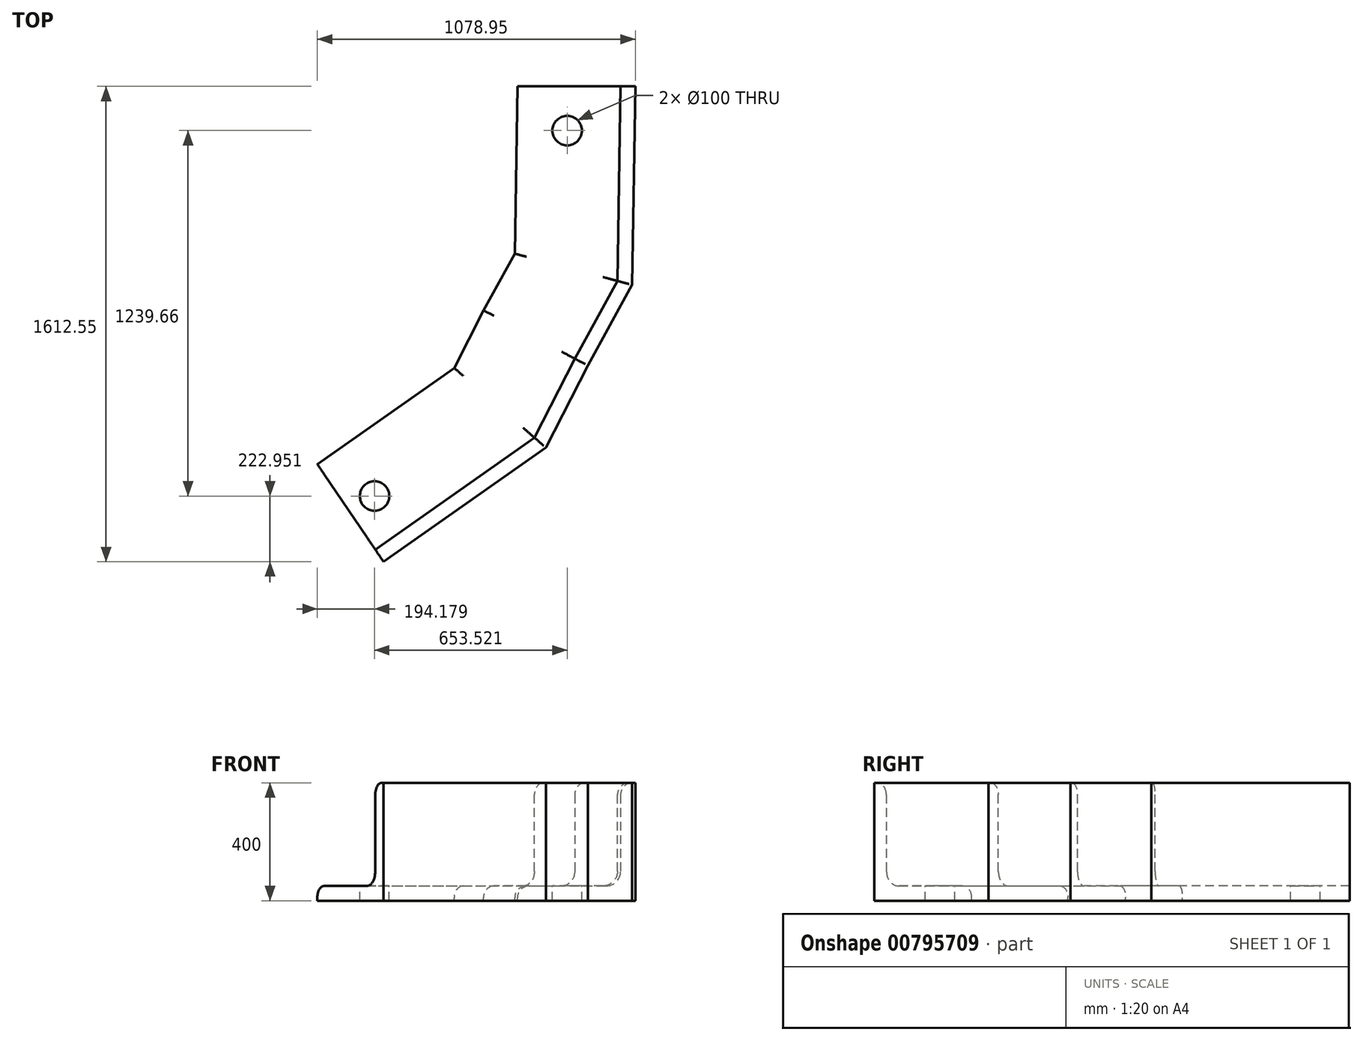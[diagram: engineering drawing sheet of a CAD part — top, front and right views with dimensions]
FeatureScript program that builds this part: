
annotation { "Feature Type Name" : "Feature", "Feature Type Description" : "" }
export const myFeature = defineFeature(function(context is Context, id is Id, definition is map)
    precondition{}
    {
        {
            var Q0;
            Q0=qCreatedBy(makeId("Front.planeOp"),FACE);
            var sketch = newSketch(context, id + "F0", { "sketchPlane" : qUnion([Q0])});
            skLineSegment(sketch, "E0", {"start": v(-836.52, 148.24) * mm, "end": v(-436.52, 148.24) * mm});
            skLineSegment(sketch, "E1", {"start": v(-436.52, 548.24) * mm, "end": v(-436.52, 148.24) * mm});
            skLineSegment(sketch, "E2.0", {"start": v(-796.52, 198.24) * mm, "end": v(-536.52, 198.24) * mm});
            skLineSegment(sketch, "E2.1", {"start": v(-486.52, 508.24) * mm, "end": v(-486.52, 248.24) * mm});
            skLineSegment(sketch, "E3", {"start": v(-436.52, 548.24) * mm, "end": v(-446.52, 548.24) * mm});
            skPoint(sketch, "E4.visualSharp", {"position": v(-486.52, 548.24) * mm});
            skArc(sketch, "E4.filletArc", {"start": v(-446.52, 548.24) * mm, "mid": v(-474.8, 536.53) * mm, "end": v(-486.52, 508.24) * mm});
            skLineSegment(sketch, "E5", {"start": v(-836.52, 148.24) * mm, "end": v(-836.52, 158.24) * mm});
            skPoint(sketch, "E6.visualSharp", {"position": v(-836.52, 198.24) * mm});
            skArc(sketch, "E6.filletArc", {"start": v(-796.52, 198.24) * mm, "mid": v(-824.8, 186.53) * mm, "end": v(-836.52, 158.24) * mm});
            skPoint(sketch, "E7.visualSharp", {"position": v(-486.52, 198.24) * mm});
            skArc(sketch, "E7.filletArc", {"start": v(-536.52, 198.24) * mm, "mid": v(-501.16, 212.89) * mm, "end": v(-486.52, 248.24) * mm});
            skSolve(sketch);
        }
        {
            var Q0;
            Q0=qCreatedBy(makeId("Top.planeOp"),FACE);
            var sketch = newSketch(context, id + "F1", { "sketchPlane" : qUnion([Q0])});
            skLineSegment(sketch, "E8", {"start": v(-107.32, -226.62) * mm, "end": v(-115.97, -761.25) * mm});
            skLineSegment(sketch, "E9", {"start": v(-115.97, -761.25) * mm, "end": v(-413.35, -1301.29) * mm});
            skSolve(sketch);
        }
        {
            var Q0;
            Q0 = qSketchRegion(id + "F0", true);
            var Q1;
            Q1 = qConstructionFilter(qBodyType(qCreatedBy(id + "F1" ,EDGE), BodyType.WIRE), ConstructionObject.NO);
            sweep(context, id + "F2", {"profiles" : qUnion([Q0]), "path" : qUnion([Q1])});
        }
        {
            var Q0;
            Q0=makeQuery(id+"F2.opSweep","SWEPT_BODY",BODY,{"disambiguationData":[OSD([sQuery(id+"F0.wireOp",EDGE,"E0"),sQuery(id+"F0.wireOp",EDGE,"E1"),sQuery(id+"F0.wireOp",EDGE,"E2.0"),sQuery(id+"F0.wireOp",EDGE,"E2.1"),sQuery(id+"F0.wireOp",EDGE,"E3"),sQuery(id+"F0.wireOp",EDGE,"E4.filletArc"),sQuery(id+"F0.wireOp",EDGE,"E5"),sQuery(id+"F0.wireOp",EDGE,"E6.filletArc"),sQuery(id+"F0.wireOp",EDGE,"E7.filletArc"),sQuery(id+"F1.wireOp",EDGE,"E9")])]});
            var Q1;
            Q1=makeQuery(id+"F2.opSweep","CAP_FACE",FACE,{"disambiguationData":[OSD([sQuery(id+"F0.wireOp",EDGE,"E0"),sQuery(id+"F0.wireOp",EDGE,"E1"),sQuery(id+"F0.wireOp",EDGE,"E2.0"),sQuery(id+"F0.wireOp",EDGE,"E2.1"),sQuery(id+"F0.wireOp",EDGE,"E3"),sQuery(id+"F0.wireOp",EDGE,"E4.filletArc"),sQuery(id+"F0.wireOp",EDGE,"E5"),sQuery(id+"F0.wireOp",EDGE,"E6.filletArc"),sQuery(id+"F0.wireOp",EDGE,"E7.filletArc"),sQuery(id+"F1.wireOp",VERTEX,"E9.end")])],"isStart":false});
            mirror(context, id + "F3", {"operationType" : NewBodyOperationType.ADD, "entities" : qUnion([Q0]), "mirrorPlane" : qUnion([Q1])});
        }
        {
            var Q0;
            {var subQ0=makeQuery(id+"F2.opSweep","SWEPT_FACE",FACE,{"disambiguationData":[OSD([sQuery(id+"F0.wireOp",EDGE,"E2.0"),sQuery(id+"F1.wireOp",EDGE,"E8")])]});Q0=makeQuery(id+"F3.boolean.opBoolean","MERGE",FACE,{"derivedFrom":[subQ0,makeQuery(id+"F3.opPattern","COPY",FACE,{"derivedFrom":subQ0,"instanceName":"1"})]});}
            var sketch = newSketch(context, id + "F4", { "sketchPlane" : qUnion([Q0])});
            skCircle(sketch, "E10", {"center": v(-667.77, -149.94) * mm, "radius": 50 * mm});
            skSolve(sketch);
        }
        {
            var Q0;
            Q0=sQuery(id+"F4.wireOp",VERTEX,"E10.center");
            var Q1;
            Q1=makeQuery(id+"F2.opSweep","SWEPT_BODY",BODY,{"disambiguationData":[OSD([sQuery(id+"F0.wireOp",EDGE,"E0"),sQuery(id+"F0.wireOp",EDGE,"E1"),sQuery(id+"F0.wireOp",EDGE,"E2.0"),sQuery(id+"F0.wireOp",EDGE,"E2.1"),sQuery(id+"F0.wireOp",EDGE,"E3"),sQuery(id+"F0.wireOp",EDGE,"E4.filletArc"),sQuery(id+"F0.wireOp",EDGE,"E5"),sQuery(id+"F0.wireOp",EDGE,"E6.filletArc"),sQuery(id+"F0.wireOp",EDGE,"E7.filletArc"),sQuery(id+"F1.wireOp",EDGE,"E9")])]});
            hole(context, id + "F5", {"style" : HoleStyle.SIMPLE, "endStyle" : HoleEndStyle.THROUGH, "holeDiameter" : 100 * mm, "majorDiameter" : 5 * mm, "isTappedThrough" : true, "tappedDepth" : 12 * mm, "tapClearance" : 3, "locations" : qUnion([Q0]), "scope" : qUnion([Q1])});
        }
        {
            var Q0;
            {var subQ0=makeQuery(id+"F2.opSweep","SWEPT_FACE",FACE,{"disambiguationData":[OSD([sQuery(id+"F0.wireOp",EDGE,"E2.0"),sQuery(id+"F1.wireOp",EDGE,"E8")])]});Q0=makeQuery(id+"F3.boolean.opBoolean","MERGE",FACE,{"derivedFrom":[subQ0,makeQuery(id+"F3.opPattern","COPY",FACE,{"derivedFrom":subQ0,"instanceName":"1"})]});}
            var sketch = newSketch(context, id + "F6", { "sketchPlane" : qUnion([Q0])});
            skLineSegment(sketch, "E11.0", {"start": v(-1321.3, -1389.6) * mm, "end": v(-936.27, -1118.99) * mm});
            skSolve(sketch);
        }
        {
            var Q0;
            Q0=sQuery(id+"F6.wireOp",VERTEX,"3796be69-d90f-4293-91cc-07bbf22c86ba.0.start");
            var Q1;
            Q1=sQuery(id+"F6.wireOp",VERTEX,"E11.0.start");
            var Q2;
            Q2=makeQuery(id+"F2.opSweep","SWEPT_BODY",BODY,{"disambiguationData":[OSD([sQuery(id+"F0.wireOp",EDGE,"E0"),sQuery(id+"F0.wireOp",EDGE,"E1"),sQuery(id+"F0.wireOp",EDGE,"E2.0"),sQuery(id+"F0.wireOp",EDGE,"E2.1"),sQuery(id+"F0.wireOp",EDGE,"E3"),sQuery(id+"F0.wireOp",EDGE,"E4.filletArc"),sQuery(id+"F0.wireOp",EDGE,"E5"),sQuery(id+"F0.wireOp",EDGE,"E6.filletArc"),sQuery(id+"F0.wireOp",EDGE,"E7.filletArc"),sQuery(id+"F1.wireOp",EDGE,"E9")])]});
            hole(context, id + "F7", {"style" : HoleStyle.SIMPLE, "endStyle" : HoleEndStyle.THROUGH, "holeDiameter" : 100 * mm, "majorDiameter" : 5 * mm, "isTappedThrough" : true, "tappedDepth" : 12 * mm, "tapClearance" : 3, "locations" : qUnion([Q0, Q1]), "scope" : qUnion([Q2])});
        }
    });
